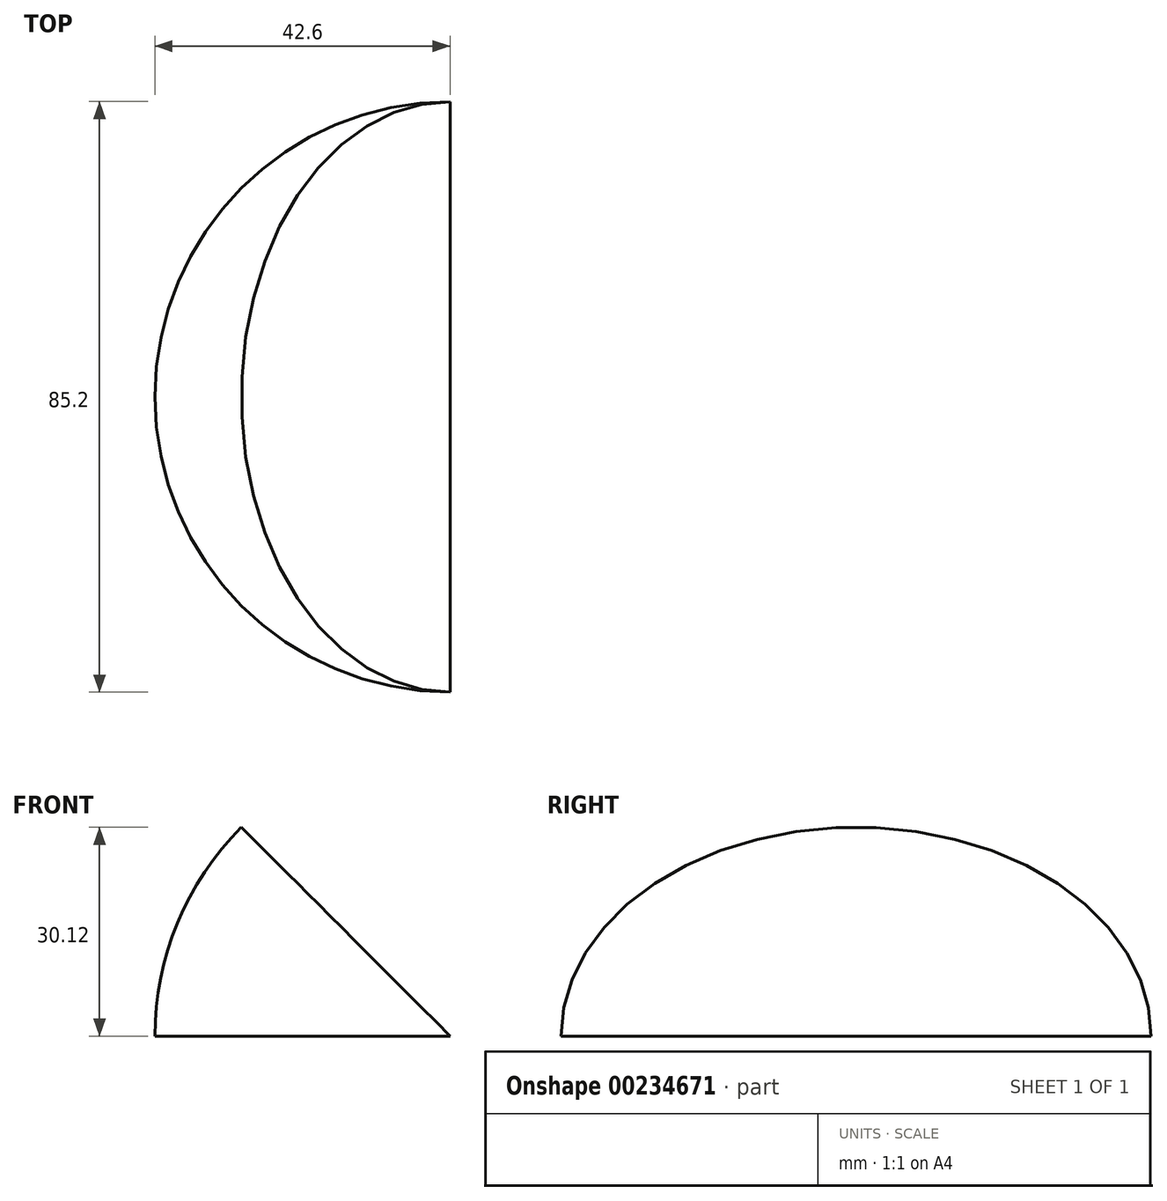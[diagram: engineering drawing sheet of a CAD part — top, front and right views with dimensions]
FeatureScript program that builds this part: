
annotation { "Feature Type Name" : "Feature", "Feature Type Description" : "" }
export const myFeature = defineFeature(function(context is Context, id is Id, definition is map)
    precondition{}
    {
        {
            var Q0;
            Q0=qCreatedBy(makeId("Top.planeOp"),FACE);
            var sketch = newSketch(context, id + "F0", { "sketchPlane" : qUnion([Q0])});
            skCircle(sketch, "E0", {"center": v(0, 0) * mm, "radius": 42.6 * mm});
            skLineSegment(sketch, "E1", {"start": v(0, 42.6) * mm, "end": v(0, -42.6) * mm});
            skSolve(sketch);
        }
        {
            var Q0;
            {var subQ0=sQuery(id+"F0.wireOp",EDGE,"E1");Q0=makeQuery(id+"F0.imprint","IMPRINT",FACE,{"disambiguationData":[TD([[makeQuery(id+"F0.imprint","IMPRINT",EDGE,{"derivedFrom":subQ0}),-1.0]])]});}
            var Q1;
            Q1=sQuery(id+"F0.wireOp",EDGE,"E1");
            revolve(context, id + "F1", {"entities" : qUnion([Q0]), "axis" : qUnion([Q1]), "revolveType" : RevolveType.ONE_DIRECTION, "oppositeDirection" : true, "angle" : 45 * degree});
        }
    });
